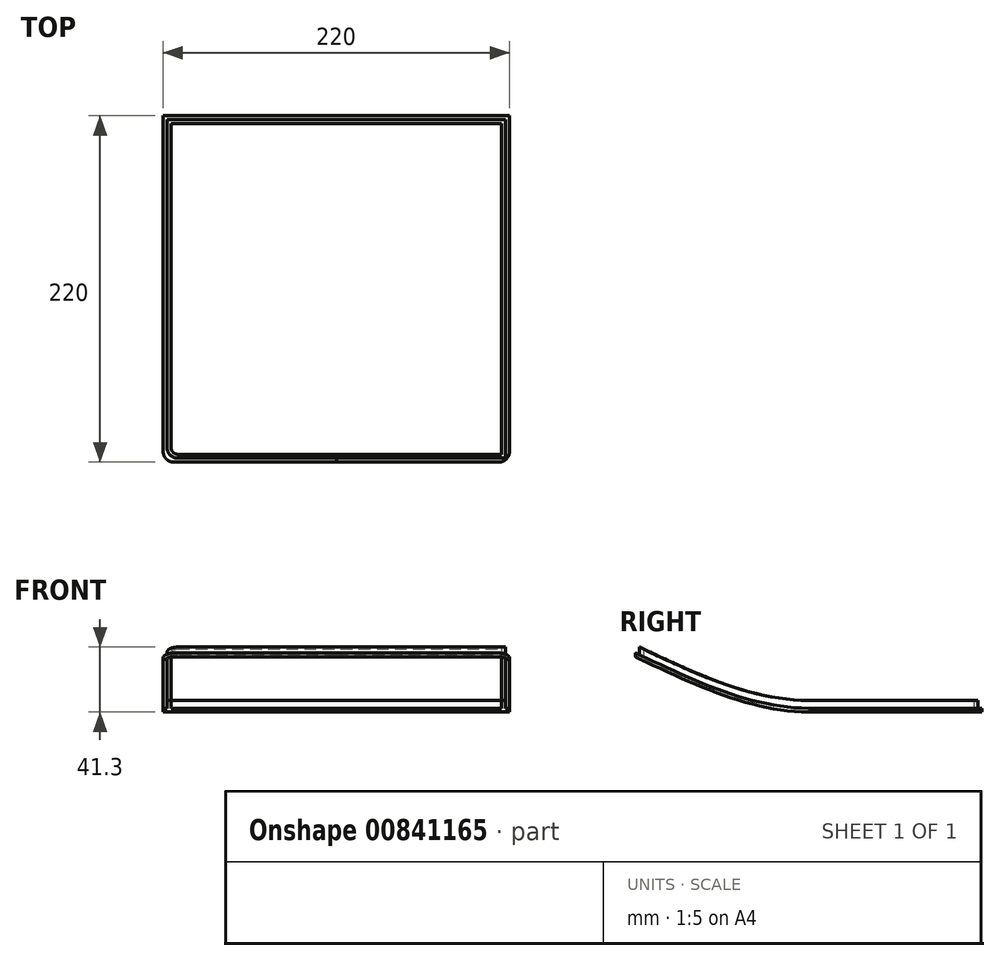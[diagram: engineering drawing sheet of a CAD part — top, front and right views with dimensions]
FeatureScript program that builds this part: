
annotation { "Feature Type Name" : "Feature", "Feature Type Description" : "" }
export const myFeature = defineFeature(function(context is Context, id is Id, definition is map)
    precondition{}
    {
        {
            var Q0;
            Q0=qCreatedBy(makeId("Top.planeOp"),FACE);
            var sketch = newSketch(context, id + "F0", { "sketchPlane" : qUnion([Q0])});
            skLineSegment(sketch, "E0.bottom", {"start": v(110, -110) * mm, "end": v(-110, -110) * mm});
            skLineSegment(sketch, "E0.top", {"start": v(110, 110) * mm, "end": v(-110, 110) * mm});
            skLineSegment(sketch, "E0.left", {"start": v(110, -110) * mm, "end": v(110, 110) * mm});
            skLineSegment(sketch, "E0.right", {"start": v(-110, -110) * mm, "end": v(-110, 110) * mm});
            skPoint(sketch, "E0.middle", {"position": v(0, 0) * mm});
            skSolve(sketch);
        }
        {
            var Q0;
            Q0=makeQuery(id+"F0.imprint","IMPRINT",FACE,{"disambiguationData":[TD([[makeQuery(id+"F0.imprint","IMPRINT",EDGE,{"derivedFrom":sQuery(id+"F0.wireOp",EDGE,"E0.bottom")}),-1.0]])]});
            var Q1;
            Q1=makeQuery(id+"F0.imprint","IMPRINT",FACE,{"disambiguationData":[TD([[makeQuery(id+"F0.imprint","IMPRINT",EDGE,{"derivedFrom":sQuery(id+"F0.wireOp",EDGE,"dqX5b5oO-QS8f-tire-DfyV-M6Jb92RfVoCi")}),1.0]])]});
            var Q2;
            Q2=makeQuery(id+"F0.imprint","IMPRINT",FACE,{"disambiguationData":[TD([[makeQuery(id+"F0.imprint","IMPRINT",EDGE,{"derivedFrom":sQuery(id+"F0.wireOp",EDGE,"rO4X43sx-pOmS-FyIm-awcV-7pWCiyp9vncQ.bottom")}),-1.0]])]});
            extrude(context, id + "F1", {"entities" : qUnion([Q0, Q1, Q2]), "depth" : 50 * mm, "offsetDistance" : 25 * mm});
        }
        {
            var Q0;
            Q0=makeQuery(id+"F1.opExtrude","SWEPT_FACE",FACE,{"disambiguationData":[OSD([sQuery(id+"F0.wireOp",EDGE,"E0.right")])]});
            var sketch = newSketch(context, id + "F2", { "sketchPlane" : qUnion([Q0])});
            skLineSegment(sketch, "E1", {"start": v(-110, 35) * mm, "end": v(110, 35) * mm, "construction": true});
            skFitSpline(sketch, "E2", {"points": [v(110, 35) * mm, v(0, 0) * mm, v(-110, 35) * mm], "startDerivative": vector(-221.3, -102.7) * mm, "endDerivative": vector(-221.08, 102.93) * mm});
            skFitSpline(sketch, "E3", {"points": [v(110, 37.5) * mm, v(0, 2.5) * mm, v(-110, 37.5) * mm], "startDerivative": vector(-223.52, -102.86) * mm, "endDerivative": vector(-222.42, 102.99) * mm});
            skLineSegment(sketch, "E4", {"start": v(0, 2.5) * mm, "end": v(-110, 2.5) * mm});
            skLineSegment(sketch, "E5", {"start": v(107.5, 50) * mm, "end": v(107.5, 36.35) * mm});
            skSolve(sketch);
        }
        {
            var Q0;
            {var subQ1=sQuery(id+"F0.wireOp",EDGE,"E0.right");var subQ2=makeQuery(id+"F1.opExtrude","SWEPT_EDGE",EDGE,{"disambiguationData":[OSD([sQuery(id+"F0.wireOp",EDGE,"E0.bottom"),subQ1])]});Q0=makeQuery(id+"F2.imprint","IMPRINT",FACE,{"disambiguationData":[TD([[makeQuery(id+"F2.imprint","IMPRINT",EDGE,{"derivedFrom":subQ2}),-1.0]])]});}
            extrude(context, id + "F3", {"entities" : qUnion([Q0]), "operationType" : NewBodyOperationType.REMOVE, "endBound" : BoundingType.THROUGH_ALL, "oppositeDirection" : true, "depth" : 25 * mm, "offsetDistance" : 25 * mm});
        }
        {
            var Q0;
            {var subQ3=sQuery(id+"F2.wireOp",EDGE,"E4");var subQ5=sQuery(id+"F2.wireOp",EDGE,"E3");var subQ7=makeQuery(id+"F2.imprint","INTERSECT",VERTEX,{"disambiguationData":[OD(1.0)],"derivedFrom":[subQ5,subQ3]});Q0=makeQuery(id+"F2.imprint","IMPRINT",FACE,{"disambiguationData":[TD([[makeQuery(id+"F2.imprint","IMPRINT",EDGE,{"disambiguationData":[TD([[subQ7,-1.0]])],"derivedFrom":subQ3}),-1.0]])]});}
            var Q1;
            {var subQ0=sQuery(id+"F2.wireOp",EDGE,"E2");var subQ3=sQuery(id+"F2.wireOp",EDGE,"E4");var subQ4=makeQuery(id+"F2.imprint","INTERSECT",VERTEX,{"derivedFrom":[subQ0,subQ3]});Q1=makeQuery(id+"F2.imprint","IMPRINT",FACE,{"disambiguationData":[TD([[makeQuery(id+"F2.imprint","IMPRINT",EDGE,{"disambiguationData":[TD([[subQ4,-1.0]])],"derivedFrom":subQ0}),1.0]])]});}
            var Q2;
            {var subQ7=sQuery(id+"F2.wireOp",EDGE,"E5");Q2=makeQuery(id+"F2.imprint","IMPRINT",FACE,{"disambiguationData":[TD([[makeQuery(id+"F2.imprint","IMPRINT",EDGE,{"derivedFrom":subQ7}),-1.0]])]});}
            extrude(context, id + "F4", {"entities" : qUnion([Q0, Q1, Q2]), "operationType" : NewBodyOperationType.REMOVE, "oppositeDirection" : true, "depth" : 2.5 * mm, "offsetDistance" : 25 * mm});
        }
        {
            var Q0;
            Q0=makeQuery(id+"F1.opExtrude","SWEPT_FACE",FACE,{"disambiguationData":[OSD([sQuery(id+"F0.wireOp",EDGE,"E0.left")])]});
            var sketch = newSketch(context, id + "F5", { "sketchPlane" : qUnion([Q0])});
            skLineSegment(sketch, "E6", {"start": v(-110, 35) * mm, "end": v(110, 35) * mm, "construction": true});
            skFitSpline(sketch, "E7", {"points": [v(110, 37.5) * mm, v(-0.09, 2.5) * mm, v(-110, 37.5) * mm], "startDerivative": vector(-221.84, -100.47) * mm, "endDerivative": vector(-220.63, 103.02) * mm});
            skFitSpline(sketch, "E8", {"points": [v(110, 35) * mm, v(0.03, 0) * mm, v(-110, 35) * mm], "startDerivative": vector(-221.92, -100.52) * mm, "endDerivative": vector(-220.95, 102.96) * mm});
            skLineSegment(sketch, "E9", {"start": v(-0.09, 2.5) * mm, "end": v(110, 2.5) * mm});
            skLineSegment(sketch, "E10", {"start": v(-107.5, 50) * mm, "end": v(-107.5, 36.33) * mm});
            skFitSpline(sketch, "E11", {"points": [v(-110, 42.5) * mm, v(0.03, 7.5) * mm, v(110, 42.5) * mm], "startDerivative": vector(215.36, -102.97) * mm, "endDerivative": vector(217.72, 100.52) * mm});
            skLineSegment(sketch, "E12", {"start": v(0.03, 7.5) * mm, "end": v(110, 7.5) * mm});
            skSolve(sketch);
        }
        {
            var Q0;
            {var subQ0=sQuery(id+"F0.wireOp",EDGE,"E0.left");var subQ1=makeQuery(id+"F1.opExtrude","CAP_EDGE",EDGE,{"disambiguationData":[OSD([subQ0])],"isStart":false});var subQ6=sQuery(id+"F5.wireOp",EDGE,"E10");var subQ7=makeQuery(id+"F5.imprint","INTERSECT",VERTEX,{"derivedFrom":[subQ1,subQ6]});Q0=makeQuery(id+"F5.imprint","IMPRINT",FACE,{"disambiguationData":[TD([[makeQuery(id+"F5.imprint","IMPRINT",EDGE,{"disambiguationData":[TD([[subQ7,-1.0]])],"derivedFrom":subQ6}),1.0]])]});}
            var Q1;
            {var subQ3=sQuery(id+"F5.wireOp",EDGE,"E12");var subQ5=sQuery(id+"F5.wireOp",EDGE,"E11");var subQ6=makeQuery(id+"F5.imprint","INTERSECT",VERTEX,{"derivedFrom":[subQ5,subQ3]});Q1=makeQuery(id+"F5.imprint","IMPRINT",FACE,{"disambiguationData":[TD([[makeQuery(id+"F5.imprint","IMPRINT",EDGE,{"disambiguationData":[TD([[subQ6,-1.0]])],"derivedFrom":subQ3}),1.0]])]});}
            var Q2;
            {var subQ0=sQuery(id+"F5.wireOp",EDGE,"E7");var subQ3=sQuery(id+"F5.wireOp",EDGE,"E12");var subQ4=makeQuery(id+"F5.imprint","INTERSECT",VERTEX,{"derivedFrom":[subQ0,subQ3]});Q2=makeQuery(id+"F5.imprint","IMPRINT",FACE,{"disambiguationData":[TD([[makeQuery(id+"F5.imprint","IMPRINT",EDGE,{"disambiguationData":[TD([[subQ4,-1.0]])],"derivedFrom":subQ3}),1.0]])]});}
            var Q3;
            {var subQ0=sQuery(id+"F5.wireOp",EDGE,"E8");var subQ3=sQuery(id+"F5.wireOp",EDGE,"E12");var subQ4=makeQuery(id+"F5.imprint","INTERSECT",VERTEX,{"derivedFrom":[subQ0,subQ3]});Q3=makeQuery(id+"F5.imprint","IMPRINT",FACE,{"disambiguationData":[TD([[makeQuery(id+"F5.imprint","IMPRINT",EDGE,{"disambiguationData":[TD([[subQ4,1.0]])],"derivedFrom":subQ0}),1.0]])]});}
            var Q4;
            {var subQ5=sQuery(id+"F5.wireOp",EDGE,"E7");var subQ6=makeQuery(id+"F5.imprint","INTERSECT",VERTEX,{"derivedFrom":[subQ5,sQuery(id+"F5.wireOp",EDGE,"E9")]});Q4=makeQuery(id+"F5.imprint","IMPRINT",FACE,{"disambiguationData":[TD([[makeQuery(id+"F5.imprint","IMPRINT",EDGE,{"disambiguationData":[TD([[subQ6,1.0]])],"derivedFrom":subQ5}),-1.0]])]});}
            var Q5;
            {var subQ0=sQuery(id+"F5.wireOp",EDGE,"E9");var subQ1=sQuery(id+"F5.wireOp",EDGE,"E7");var subQ2=makeQuery(id+"F5.imprint","INTERSECT",VERTEX,{"derivedFrom":[subQ1,subQ0]});Q5=makeQuery(id+"F5.imprint","IMPRINT",FACE,{"disambiguationData":[TD([[makeQuery(id+"F5.imprint","IMPRINT",EDGE,{"disambiguationData":[TD([[subQ2,1.0]])],"derivedFrom":subQ1}),1.0]])]});}
            var Q6;
            {var subQ0=sQuery(id+"F5.wireOp",EDGE,"E12");var subQ1=sQuery(id+"F5.wireOp",EDGE,"E8");var subQ2=makeQuery(id+"F5.imprint","INTERSECT",VERTEX,{"derivedFrom":[subQ1,subQ0]});Q6=makeQuery(id+"F5.imprint","IMPRINT",FACE,{"disambiguationData":[TD([[makeQuery(id+"F5.imprint","IMPRINT",EDGE,{"disambiguationData":[TD([[subQ2,-1.0]])],"derivedFrom":subQ1}),1.0]])]});}
            extrude(context, id + "F6", {"entities" : qUnion([Q0, Q1, Q2, Q3, Q4, Q5, Q6]), "operationType" : NewBodyOperationType.REMOVE, "oppositeDirection" : true, "depth" : 2.5 * mm, "offsetDistance" : 25 * mm});
        }
        {
            var Q0;
            {var subQ0=sQuery(id+"F0.wireOp",EDGE,"E0.left");var subQ1=makeQuery(id+"F1.opExtrude","CAP_EDGE",EDGE,{"disambiguationData":[OSD([subQ0])],"isStart":false});var subQ6=sQuery(id+"F5.wireOp",EDGE,"E10");var subQ7=makeQuery(id+"F5.imprint","INTERSECT",VERTEX,{"derivedFrom":[subQ1,subQ6]});Q0=makeQuery(id+"F5.imprint","IMPRINT",FACE,{"disambiguationData":[TD([[makeQuery(id+"F5.imprint","IMPRINT",EDGE,{"disambiguationData":[TD([[subQ7,-1.0]])],"derivedFrom":subQ6}),1.0]])]});}
            var Q1;
            {var subQ3=sQuery(id+"F5.wireOp",EDGE,"E12");var subQ5=sQuery(id+"F5.wireOp",EDGE,"E11");var subQ6=makeQuery(id+"F5.imprint","INTERSECT",VERTEX,{"derivedFrom":[subQ5,subQ3]});Q1=makeQuery(id+"F5.imprint","IMPRINT",FACE,{"disambiguationData":[TD([[makeQuery(id+"F5.imprint","IMPRINT",EDGE,{"disambiguationData":[TD([[subQ6,-1.0]])],"derivedFrom":subQ3}),1.0]])]});}
            var Q2;
            {var subQ0=sQuery(id+"F5.wireOp",EDGE,"E7");var subQ3=sQuery(id+"F5.wireOp",EDGE,"E12");var subQ4=makeQuery(id+"F5.imprint","INTERSECT",VERTEX,{"derivedFrom":[subQ0,subQ3]});Q2=makeQuery(id+"F5.imprint","IMPRINT",FACE,{"disambiguationData":[TD([[makeQuery(id+"F5.imprint","IMPRINT",EDGE,{"disambiguationData":[TD([[subQ4,-1.0]])],"derivedFrom":subQ3}),1.0]])]});}
            var Q3;
            {var subQ0=sQuery(id+"F5.wireOp",EDGE,"E8");var subQ3=sQuery(id+"F5.wireOp",EDGE,"E12");var subQ4=makeQuery(id+"F5.imprint","INTERSECT",VERTEX,{"derivedFrom":[subQ0,subQ3]});Q3=makeQuery(id+"F5.imprint","IMPRINT",FACE,{"disambiguationData":[TD([[makeQuery(id+"F5.imprint","IMPRINT",EDGE,{"disambiguationData":[TD([[subQ4,1.0]])],"derivedFrom":subQ0}),1.0]])]});}
            extrude(context, id + "F7", {"entities" : qUnion([Q0, Q1, Q2, Q3]), "operationType" : NewBodyOperationType.REMOVE, "endBound" : BoundingType.THROUGH_ALL, "oppositeDirection" : true, "depth" : 25 * mm, "offsetDistance" : 25 * mm});
        }
        {
            var Q0;
            Q0=makeQuery(id+"F1.opExtrude","SWEPT_FACE",FACE,{"disambiguationData":[OSD([sQuery(id+"F0.wireOp",EDGE,"E0.top")])]});
            var sketch = newSketch(context, id + "F8", { "sketchPlane" : qUnion([Q0])});
            skLineSegment(sketch, "E13", {"start": v(107.5, 2.5) * mm, "end": v(-110, 2.5) * mm});
            skSolve(sketch);
        }
        {
            var Q0;
            {var subQ0=sQuery(id+"F8.wireOp",EDGE,"E13");Q0=makeQuery(id+"F8.imprint","IMPRINT",FACE,{"disambiguationData":[TD([[makeQuery(id+"F8.imprint","IMPRINT",EDGE,{"derivedFrom":subQ0}),-1.0]])]});}
            extrude(context, id + "F9", {"entities" : qUnion([Q0]), "operationType" : NewBodyOperationType.REMOVE, "oppositeDirection" : true, "depth" : 2.5 * mm, "offsetDistance" : 25 * mm});
        }
        {
            var Q0;
            {var subQ4=sQuery(id+"F5.wireOp",EDGE,"E10");Q0=makeQuery(id+"F5.imprint","IMPRINT",FACE,{"disambiguationData":[TD([[makeQuery(id+"F5.imprint","IMPRINT",EDGE,{"derivedFrom":subQ4}),-1.0]])]});}
            extrude(context, id + "F10", {"entities" : qUnion([Q0]), "operationType" : NewBodyOperationType.REMOVE, "oppositeDirection" : true, "depth" : (220 / 2) * mm, "offsetDistance" : 25 * mm});
        }
        {
            var Q0;
            {var subQ4=sQuery(id+"F2.wireOp",EDGE,"E5");Q0=makeQuery(id+"F2.imprint","IMPRINT",FACE,{"disambiguationData":[TD([[makeQuery(id+"F2.imprint","IMPRINT",EDGE,{"derivedFrom":subQ4}),1.0]])]});}
            extrude(context, id + "F11", {"entities" : qUnion([Q0]), "operationType" : NewBodyOperationType.REMOVE, "oppositeDirection" : true, "depth" : (220 / 2) * mm, "offsetDistance" : 25 * mm});
        }
        {
            var Q0;
            Q0=makeQuery(id+"F6.boolean.opBoolean","COPY",EDGE,{"derivedFrom":makeQuery(id+"F6.opExtrude","CAP_EDGE",EDGE,{"disambiguationData":[OSD([sQuery(id+"F5.wireOp",EDGE,"E10")])],"isStart":false})});
            var Q1;
            Q1=makeQuery(id+"F1.opExtrude","SWEPT_EDGE",EDGE,{"disambiguationData":[OSD([sQuery(id+"F0.wireOp",EDGE,"E0.bottom"),sQuery(id+"F0.wireOp",EDGE,"E0.left")])]});
            var Q2;
            Q2=makeQuery(id+"F4.boolean.opBoolean","COPY",EDGE,{"derivedFrom":makeQuery(id+"F4.opExtrude","CAP_EDGE",EDGE,{"disambiguationData":[OSD([sQuery(id+"F2.wireOp",EDGE,"E5")])],"isStart":false})});
            var Q3;
            Q3=makeQuery(id+"F1.opExtrude","SWEPT_EDGE",EDGE,{"disambiguationData":[OSD([sQuery(id+"F0.wireOp",EDGE,"E0.bottom"),sQuery(id+"F0.wireOp",EDGE,"E0.right")])]});
            fillet(context, id + "F12", {"entities" : qUnion([Q0, Q1, Q2, Q3]), "radius" : (13.5 / 2) * mm, "allowEdgeOverflow" : false});
        }
        {
            var Q0;
            Q0=makeQuery(id+"F7.boolean.opBoolean","COPY",FACE,{"derivedFrom":makeQuery(id+"F7.opExtrude","SWEPT_FACE",FACE,{"disambiguationData":[OSD([sQuery(id+"F5.wireOp",EDGE,"E11")])]})});
            var Q1;
            Q1=makeQuery(id+"F7.boolean.opBoolean","COPY",FACE,{"derivedFrom":makeQuery(id+"F7.opExtrude","SWEPT_FACE",FACE,{"disambiguationData":[OSD([sQuery(id+"F5.wireOp",EDGE,"E12")])]})});
            shell(context, id + "F13", {"entities" : qUnion([Q0, Q1]), "thickness" : 2.5 * mm});
        }
    });
